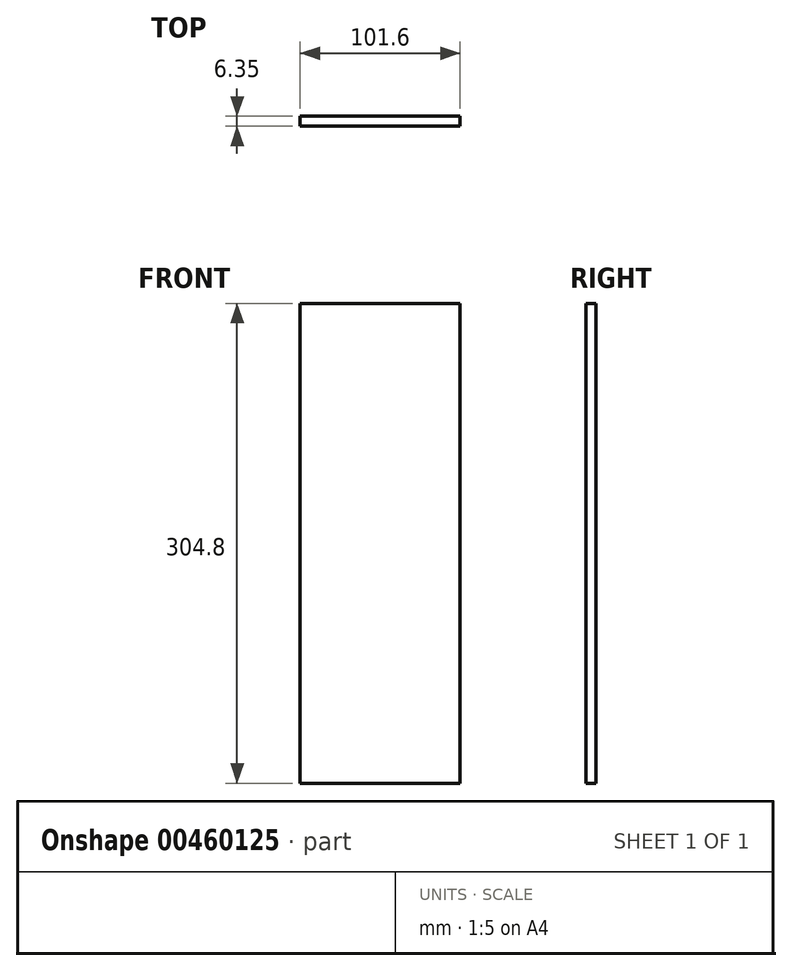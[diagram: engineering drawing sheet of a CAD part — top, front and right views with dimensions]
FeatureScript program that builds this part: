
annotation { "Feature Type Name" : "Feature", "Feature Type Description" : "" }
export const myFeature = defineFeature(function(context is Context, id is Id, definition is map)
    precondition{}
    {
        {
            var Q0;
            Q0=qCreatedBy(makeId("Front.planeOp"),FACE);
            var sketch = newSketch(context, id + "F0", { "sketchPlane" : qUnion([Q0])});
            skLineSegment(sketch, "E0.bottom", {"start": v(0, 0) * mm, "end": v(101.6, 0) * mm});
            skLineSegment(sketch, "E0.top", {"start": v(0, 304.8) * mm, "end": v(101.6, 304.8) * mm});
            skLineSegment(sketch, "E0.left", {"start": v(0, 0) * mm, "end": v(0, 304.8) * mm});
            skLineSegment(sketch, "E0.right", {"start": v(101.6, 0) * mm, "end": v(101.6, 304.8) * mm});
            skSolve(sketch);
        }
        {
            var Q0;
            Q0=makeQuery(id+"F0.imprint","IMPRINT",FACE,{"disambiguationData":[TD([[makeQuery(id+"F0.imprint","IMPRINT",EDGE,{"derivedFrom":sQuery(id+"F0.wireOp",EDGE,"E0.bottom")}),1.0]])]});
            extrude(context, id + "F1", {"entities" : qUnion([Q0]), "depth" : 6.35 * mm});
        }
    });
